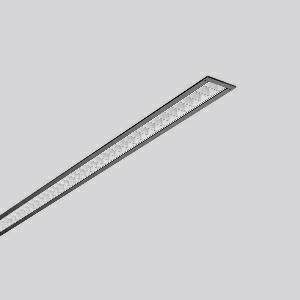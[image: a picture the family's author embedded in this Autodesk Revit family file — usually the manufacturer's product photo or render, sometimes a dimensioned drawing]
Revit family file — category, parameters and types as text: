
# Revit family: less_is_more_27_312179_003_1_baf3
name_source: partatom
category: Lighting Fixtures
units: mm (PartAtom-declared; Revit-internal decimal feet)

## family parameters
Cut with Voids When Loaded = No
Host = Face
Light Source = No
Part Type = Normal
Room Calculation Point = No
Round Connector Dimension = Use Diameter
Shared = No

## types (1)
- LESS IS MORE 27 (1 x LED Modul 840, 3500 lm, 4000)
    Apparent Load = 39 VA
    CIE Flux Codes = 90 99 100 100 100
    Color Rendering = 80
    Color Temperature = 4000
    Default Elevation = 1800 mm
    Description = Series: LESS IS MORE 27
Recessed ceiling and wall luminaire with slim design. Housing: extruded aluminium profile, powder-coated. End cap aluminium powder-coated. High polish aluminium micro grid. Perfect for office areas (RUG < 19) and environments with computer screens in accordance with EN 12464-1. Suitable for Recessed ceiling mounting, wall (recessed). External driver with connecting cable. 
Colour: deep black, matt (RAL 9005)
Length: 1514 mm
Width: 38 mm
Height: 2 mm
Cut-out length: 1506 mm
Cut-out width: 30 mm
Recess height: 45-60 mm
Luminaire: recess height: 37 mm
Lamp: LED
Socket: without socket
Colour temperature: 4000K
Colour rendering index (CRI): 82
System power: 39 W
Rated luminous flux: 3500 lm
Luminous efficiency: 90 lm/W
Control gear: Regulated power supply
Protection class: II
Type of protection: IP 20
    Height = 0 mm  [stored 0 ft]
    Lamp = 1 x LED Modul 840
    Lamp Light Flux = 3500 lm
    Lamp count = 1
    Length = 1514 mm
    Lifetime = 50000 h
    Luminous efficacy = 90 lm/W
    Manufacturer = RZB
    ModVariant = No
    Model = 312179.003.1
    Mounting Place = Ceiling, Wall
    Mounting Type = Recessed
    Number of Poles = 1
    OnlyDefault = Yes
    Power Factor = 1
    Product Name = LESS IS MORE 27
    Product group = Recessed LED linear luminaires
    ProductGroupID = 407
    Protection Class = Protection class II
    Protection Degree = IP 20
    RLX_Detail_Level = 1
    RLX_Emergency_Light_Flux = 0 lm
    RLX_Emergency_Type = 0
    RLX_Emergency_Type_DB = No
    RlxData = <blob elided: 29905 chars, md5=d1cb6462>
    Socket = socket
    Standby Power = 0 W
    System Light Flux = 3500 lm
    System Power = 39 W
    Type Comments = Product without accessories
    Type Image = 312177.003.jpg
    URL = http://relux.com
    VarID = ---
    Voltage = 230 V
    Voltage Range = 220-240 V
    Weight = 0.00 kg
    Width = 38 mm

note: [stored X ft] marks values corroborated as IEEE doubles in the binary element streams (Revit-internal decimal feet)

## geometry (parser evidence)
native form markers: Blend x4, Sweep x11
no freeform markers — native parametric forms only
